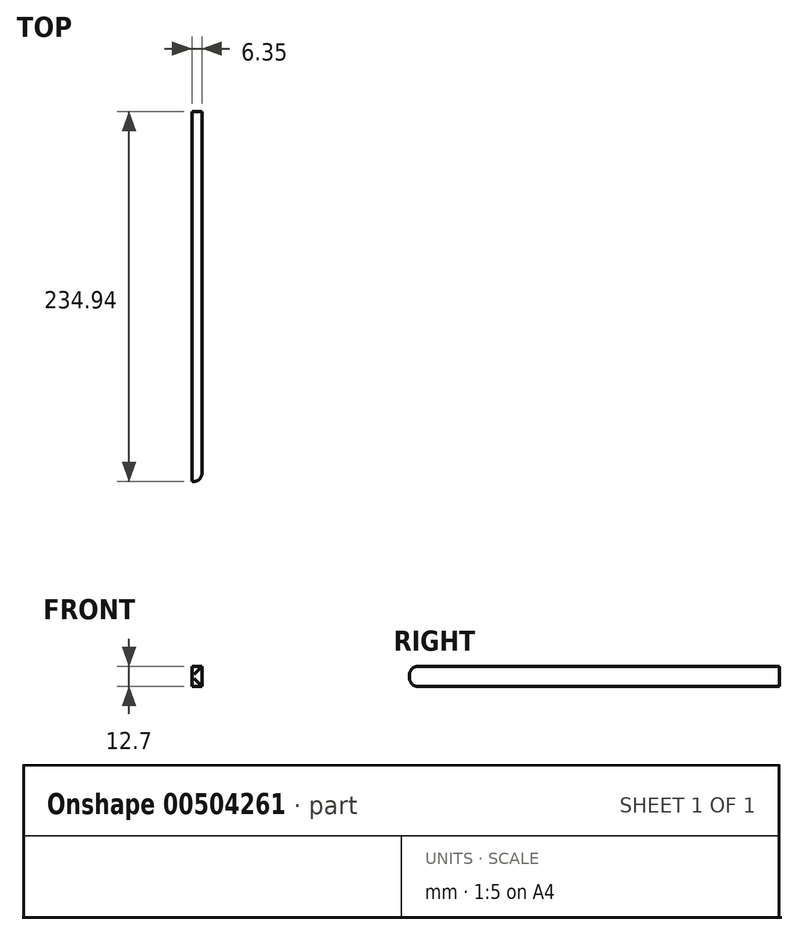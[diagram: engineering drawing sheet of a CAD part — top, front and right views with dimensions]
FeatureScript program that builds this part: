
annotation { "Feature Type Name" : "Feature", "Feature Type Description" : "" }
export const myFeature = defineFeature(function(context is Context, id is Id, definition is map)
    precondition{}
    {
        {
            var Q0;
            Q0=qCreatedBy(makeId("Right.planeOp"),FACE);
            var sketch = newSketch(context, id + "F0", { "sketchPlane" : qUnion([Q0])});
            skLineSegment(sketch, "E0.bottom", {"start": v(117.48, -6.35) * mm, "end": v(-117.48, -6.35) * mm});
            skLineSegment(sketch, "E0.top", {"start": v(117.48, 6.35) * mm, "end": v(-117.48, 6.35) * mm});
            skLineSegment(sketch, "E0.left", {"start": v(117.48, -6.35) * mm, "end": v(117.48, 6.35) * mm});
            skLineSegment(sketch, "E0.right", {"start": v(-117.48, -6.35) * mm, "end": v(-117.48, 6.35) * mm});
            skPoint(sketch, "E0.middle", {"position": v(0, 0) * mm});
            skPoint(sketch, "E1", {"position": v(-117.48, 6.35) * mm});
            skPoint(sketch, "E2", {"position": v(-117.48, -6.35) * mm});
            skSolve(sketch);
        }
        {
            var Q0;
            Q0=makeQuery(id+"F0.imprint","IMPRINT",FACE,{"disambiguationData":[TD([[makeQuery(id+"F0.imprint","IMPRINT",EDGE,{"derivedFrom":sQuery(id+"F0.wireOp",EDGE,"E0.bottom")}),-1.0]])]});
            extrude(context, id + "F1", {"entities" : qUnion([Q0]), "depth" : 6.35 * mm});
        }
        {
            var Q0;
            Q0=makeQuery(id+"F1.opExtrude","SWEPT_EDGE",EDGE,{"disambiguationData":[OSD([sQuery(id+"F0.wireOp",EDGE,"E0.top"),sQuery(id+"F0.wireOp",EDGE,"E0.right")])]});
            var Q1;
            Q1=makeQuery(id+"F1.opExtrude","CAP_EDGE",EDGE,{"disambiguationData":[OSD([sQuery(id+"F0.wireOp",EDGE,"E0.right")])],"isStart":false});
            var Q2;
            Q2=makeQuery(id+"F1.opExtrude","SWEPT_EDGE",EDGE,{"disambiguationData":[OSD([sQuery(id+"F0.wireOp",EDGE,"E0.bottom"),sQuery(id+"F0.wireOp",EDGE,"E0.right")])]});
            fillet(context, id + "F2", {"entities" : qUnion([Q0, Q1, Q2]), "radius" : 5.08 * mm, "tangentPropagation" : true, "allowEdgeOverflow" : false});
        }
    });
